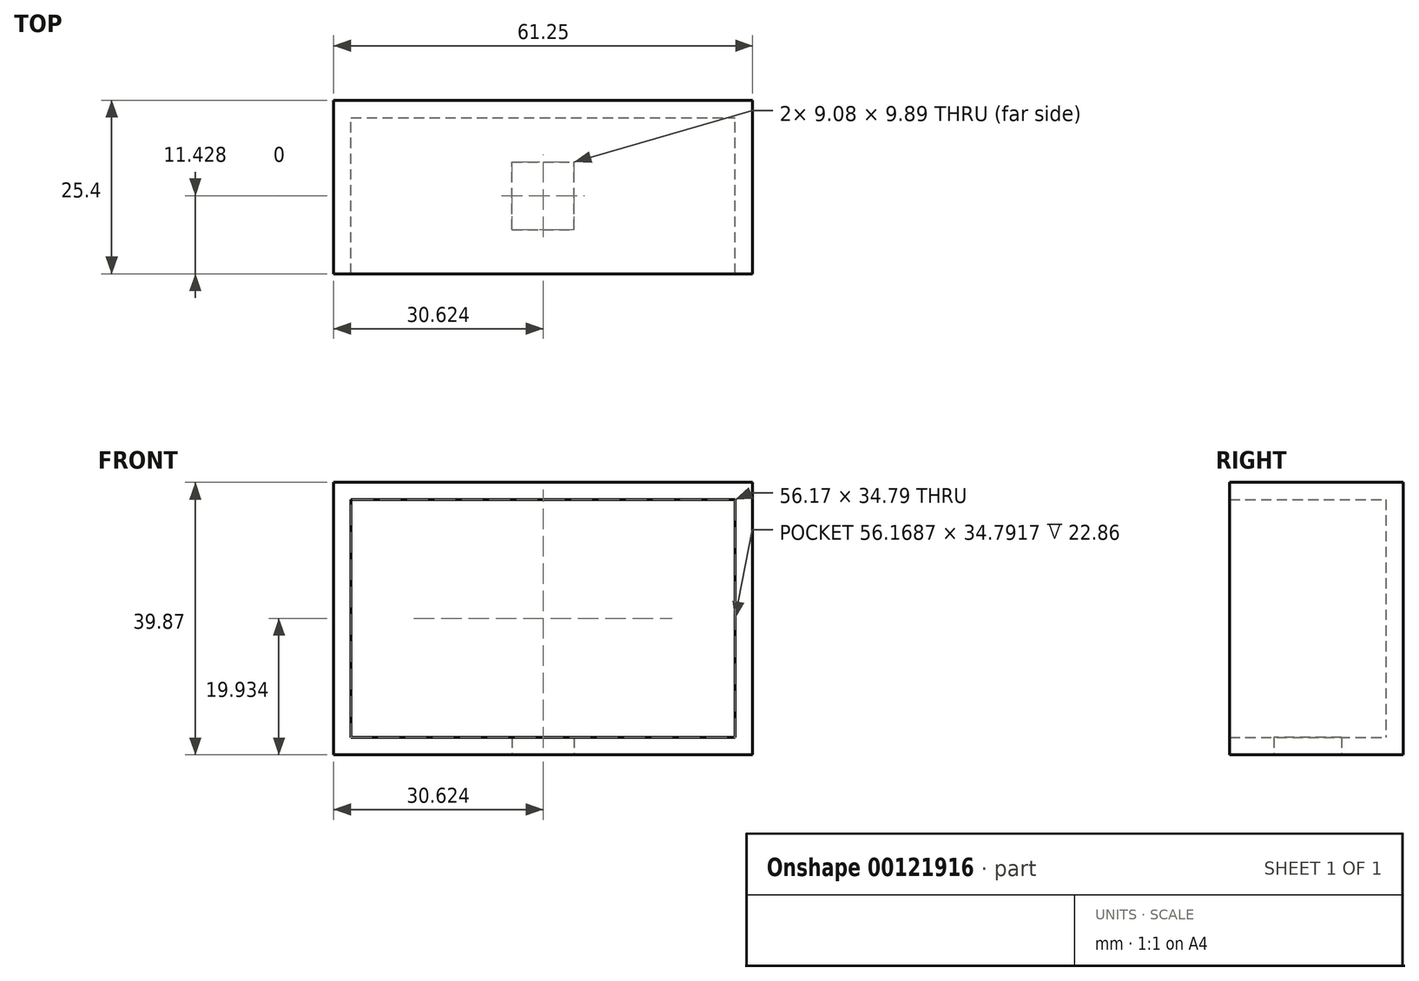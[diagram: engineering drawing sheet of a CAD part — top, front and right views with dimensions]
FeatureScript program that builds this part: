
annotation { "Feature Type Name" : "Feature", "Feature Type Description" : "" }
export const myFeature = defineFeature(function(context is Context, id is Id, definition is map)
    precondition{}
    {
        {
            var Q0;
            Q0=qCreatedBy(makeId("Front.planeOp"),FACE);
            var sketch = newSketch(context, id + "F0", { "sketchPlane" : qUnion([Q0])});
            skLineSegment(sketch, "E0.bottom", {"start": v(0, 0) * mm, "end": v(61.25, 0) * mm});
            skLineSegment(sketch, "E0.top", {"start": v(0, -39.87) * mm, "end": v(61.25, -39.87) * mm});
            skLineSegment(sketch, "E0.left", {"start": v(0, 0) * mm, "end": v(0, -39.87) * mm});
            skLineSegment(sketch, "E0.right", {"start": v(61.25, 0) * mm, "end": v(61.25, -39.87) * mm});
            skSolve(sketch);
        }
        {
            var Q0;
            Q0 = qSketchRegion(id + "F0", true);
            extrude(context, id + "F1", {"entities" : qUnion([Q0]), "depth" : 25.4 * mm});
        }
        {
            var Q0;
            Q0=makeQuery(id+"F1.opExtrude","CAP_FACE",FACE,{"disambiguationData":[OSD([sQuery(id+"F0.wireOp",EDGE,"E0.bottom"),sQuery(id+"F0.wireOp",EDGE,"E0.top"),sQuery(id+"F0.wireOp",EDGE,"E0.left"),sQuery(id+"F0.wireOp",EDGE,"E0.right")])],"isStart":false});
            shell(context, id + "F2", {"entities" : qUnion([Q0]), "thickness" : 2.54 * mm});
        }
        {
            var Q0;
            Q0=makeQuery(id+"F1.opExtrude","SWEPT_FACE",FACE,{"disambiguationData":[OSD([sQuery(id+"F0.wireOp",EDGE,"E0.top")])]});
            var sketch = newSketch(context, id + "F3", { "sketchPlane" : qUnion([Q0])});
            skLineSegment(sketch, "E1.bottom", {"start": v(26.08, 18.92) * mm, "end": v(35.16, 18.92) * mm});
            skLineSegment(sketch, "E1.top", {"start": v(26.08, 9.03) * mm, "end": v(35.16, 9.03) * mm});
            skLineSegment(sketch, "E1.left", {"start": v(26.08, 18.92) * mm, "end": v(26.08, 9.03) * mm});
            skLineSegment(sketch, "E1.right", {"start": v(35.16, 18.92) * mm, "end": v(35.16, 9.03) * mm});
            skPoint(sketch, "E2", {"position": v(30.62, 18.92) * mm});
            skPoint(sketch, "E3", {"position": v(30.62, 25.4) * mm});
            skSolve(sketch);
        }
        {
            var Q0;
            Q0 = qSketchRegion(id + "F3", true);
            extrude(context, id + "F4", {"entities" : qUnion([Q0]), "operationType" : NewBodyOperationType.REMOVE, "oppositeDirection" : true, "depth" : 25.4 * mm});
        }
    });
